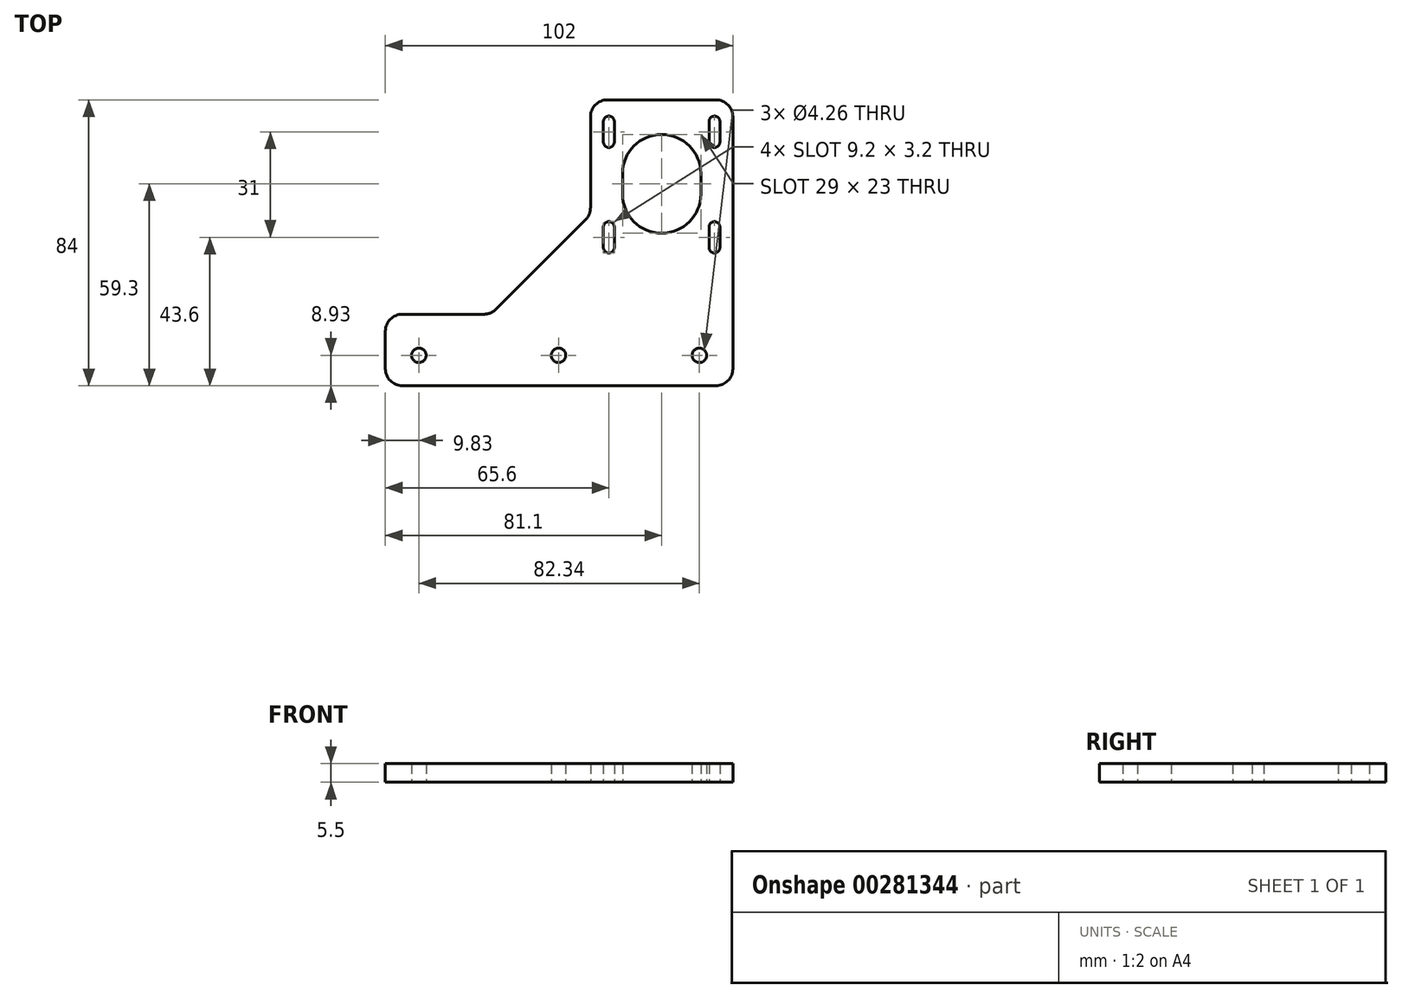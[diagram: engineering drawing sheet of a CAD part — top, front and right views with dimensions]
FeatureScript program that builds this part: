
annotation { "Feature Type Name" : "Feature", "Feature Type Description" : "" }
export const myFeature = defineFeature(function(context is Context, id is Id, definition is map)
    precondition{}
    {
        {
            var Q0;
            Q0=qCreatedBy(makeId("Top.planeOp"),FACE);
            var sketch = newSketch(context, id + "F0", { "sketchPlane" : qUnion([Q0])});
            skArc(sketch, "E0", {"start": v(16.2, 35.6) * mm, "mid": v(14.6, 37.2) * mm, "end": v(13, 35.6) * mm});
            skLineSegment(sketch, "E1", {"start": v(13, 35.6) * mm, "end": v(13, 29.6) * mm});
            skArc(sketch, "E2", {"start": v(13, 29.6) * mm, "mid": v(14.6, 28) * mm, "end": v(16.2, 29.6) * mm});
            skLineSegment(sketch, "E3", {"start": v(16.2, 29.6) * mm, "end": v(16.2, 35.6) * mm});
            skArc(sketch, "E4", {"start": v(7.74, 6.74) * mm, "mid": v(8.82, 8.36) * mm, "end": v(9.2, 10.27) * mm});
            skLineSegment(sketch, "E5", {"start": v(9.2, 10.27) * mm, "end": v(9.2, 37) * mm});
            skArc(sketch, "E6", {"start": v(9.2, 37) * mm, "mid": v(10.67, 40.53) * mm, "end": v(14.2, 42) * mm});
            skLineSegment(sketch, "E7", {"start": v(14.2, 42) * mm, "end": v(46, 42) * mm});
            skArc(sketch, "E8", {"start": v(46, 42) * mm, "mid": v(49.53, 40.53) * mm, "end": v(51, 37) * mm});
            skLineSegment(sketch, "E9", {"start": v(51, 37) * mm, "end": v(51, -37) * mm});
            skArc(sketch, "E10", {"start": v(51, -37) * mm, "mid": v(49.53, -40.53) * mm, "end": v(46, -42) * mm});
            skLineSegment(sketch, "E11", {"start": v(46, -42) * mm, "end": v(-46, -42) * mm});
            skArc(sketch, "E12", {"start": v(-46, -42) * mm, "mid": v(-49.53, -40.53) * mm, "end": v(-51, -37) * mm});
            skLineSegment(sketch, "E13", {"start": v(-51, -37) * mm, "end": v(-51, -26) * mm});
            skArc(sketch, "E14", {"start": v(-51, -26) * mm, "mid": v(-49.53, -22.47) * mm, "end": v(-46, -21) * mm});
            skLineSegment(sketch, "E15", {"start": v(-46, -21) * mm, "end": v(-22.07, -21) * mm});
            skArc(sketch, "E16", {"start": v(-22.07, -21) * mm, "mid": v(-20.16, -20.62) * mm, "end": v(-18.54, -19.54) * mm});
            skLineSegment(sketch, "E17", {"start": v(-18.54, -19.54) * mm, "end": v(7.74, 6.74) * mm});
            skLineSegment(sketch, "E18", {"start": v(47.2, 29.6) * mm, "end": v(47.2, 35.6) * mm});
            skArc(sketch, "E19", {"start": v(47.2, 35.6) * mm, "mid": v(45.6, 37.2) * mm, "end": v(44, 35.6) * mm});
            skLineSegment(sketch, "E20", {"start": v(44, 35.6) * mm, "end": v(44, 29.6) * mm});
            skArc(sketch, "E21", {"start": v(44, 29.6) * mm, "mid": v(45.6, 28) * mm, "end": v(47.2, 29.6) * mm});
            skArc(sketch, "E22", {"start": v(18.6, 14.3) * mm, "mid": v(30.1, 2.8) * mm, "end": v(41.6, 14.3) * mm});
            skLineSegment(sketch, "E23", {"start": v(41.6, 14.3) * mm, "end": v(41.6, 20.3) * mm});
            skArc(sketch, "E24", {"start": v(41.6, 20.3) * mm, "mid": v(30.1, 31.8) * mm, "end": v(18.6, 20.3) * mm});
            skLineSegment(sketch, "E25", {"start": v(18.6, 20.3) * mm, "end": v(18.6, 14.3) * mm});
            skCircle(sketch, "E26", {"center": v(41.17, -33.07) * mm, "radius": 2.13 * mm});
            skArc(sketch, "E27", {"start": v(16.2, 4.6) * mm, "mid": v(14.6, 6.2) * mm, "end": v(13, 4.6) * mm});
            skLineSegment(sketch, "E28", {"start": v(13, 4.6) * mm, "end": v(13, -1.4) * mm});
            skArc(sketch, "E29", {"start": v(13, -1.4) * mm, "mid": v(14.6, -3) * mm, "end": v(16.2, -1.4) * mm});
            skLineSegment(sketch, "E30", {"start": v(16.2, -1.4) * mm, "end": v(16.2, 4.6) * mm});
            skLineSegment(sketch, "E31", {"start": v(47.2, -1.4) * mm, "end": v(47.2, 4.6) * mm});
            skArc(sketch, "E32", {"start": v(47.2, 4.6) * mm, "mid": v(45.6, 6.2) * mm, "end": v(44, 4.6) * mm});
            skLineSegment(sketch, "E33", {"start": v(44, 4.6) * mm, "end": v(44, -1.4) * mm});
            skArc(sketch, "E34", {"start": v(44, -1.4) * mm, "mid": v(45.6, -3) * mm, "end": v(47.2, -1.4) * mm});
            skCircle(sketch, "E35", {"center": v(-0.17, -33.07) * mm, "radius": 2.13 * mm});
            skCircle(sketch, "E36", {"center": v(-41.17, -33.07) * mm, "radius": 2.13 * mm});
            skSolve(sketch);
        }
        {
            var Q0;
            Q0=makeQuery(id+"F0.imprint","IMPRINT",FACE,{"disambiguationData":[TD([[makeQuery(id+"F0.imprint","IMPRINT",EDGE,{"derivedFrom":sQuery(id+"F0.wireOp",EDGE,"E0")}),-1.0]])]});
            var Q1;
            Q1=sQuery(id+"F0.wireOp",EDGE,"E17");
            var Q2;
            Q2=sQuery(id+"F0.wireOp",EDGE,"E16");
            var Q3;
            Q3=sQuery(id+"F0.wireOp",EDGE,"E15");
            var Q4;
            Q4=sQuery(id+"F0.wireOp",EDGE,"E14");
            var Q5;
            Q5=sQuery(id+"F0.wireOp",EDGE,"E13");
            var Q6;
            Q6=sQuery(id+"F0.wireOp",EDGE,"E12");
            var Q7;
            Q7=sQuery(id+"F0.wireOp",EDGE,"E11");
            var Q8;
            Q8=sQuery(id+"F0.wireOp",EDGE,"E9");
            var Q9;
            Q9=sQuery(id+"F0.wireOp",EDGE,"E8");
            var Q10;
            Q10=sQuery(id+"F0.wireOp",EDGE,"E10");
            var Q11;
            Q11=sQuery(id+"F0.wireOp",EDGE,"E6");
            var Q12;
            Q12=sQuery(id+"F0.wireOp",EDGE,"E7");
            var Q13;
            Q13=sQuery(id+"F0.wireOp",EDGE,"E5");
            var Q14;
            Q14=sQuery(id+"F0.wireOp",EDGE,"E4");
            var Q15;
            Q15=sQuery(id+"F0.wireOp",EDGE,"E24");
            var Q16;
            Q16=sQuery(id+"F0.wireOp",EDGE,"E22");
            var Q17;
            Q17=sQuery(id+"F0.wireOp",EDGE,"E23");
            var Q18;
            Q18=sQuery(id+"F0.wireOp",EDGE,"E25");
            var Q19;
            Q19=sQuery(id+"F0.wireOp",EDGE,"E2");
            var Q20;
            Q20=sQuery(id+"F0.wireOp",EDGE,"E3");
            var Q21;
            Q21=sQuery(id+"F0.wireOp",EDGE,"E0");
            var Q22;
            Q22=sQuery(id+"F0.wireOp",EDGE,"E1");
            var Q23;
            Q23=sQuery(id+"F0.wireOp",EDGE,"E29");
            var Q24;
            Q24=sQuery(id+"F0.wireOp",EDGE,"E30");
            var Q25;
            Q25=sQuery(id+"F0.wireOp",EDGE,"E27");
            var Q26;
            Q26=sQuery(id+"F0.wireOp",EDGE,"E28");
            var Q27;
            Q27=sQuery(id+"F0.wireOp",EDGE,"E34");
            var Q28;
            Q28=sQuery(id+"F0.wireOp",EDGE,"E31");
            var Q29;
            Q29=sQuery(id+"F0.wireOp",EDGE,"E33");
            var Q30;
            Q30=sQuery(id+"F0.wireOp",EDGE,"E32");
            var Q31;
            Q31=sQuery(id+"F0.wireOp",EDGE,"E18");
            var Q32;
            Q32=sQuery(id+"F0.wireOp",EDGE,"E20");
            var Q33;
            Q33=sQuery(id+"F0.wireOp",EDGE,"E19");
            var Q34;
            Q34=sQuery(id+"F0.wireOp",EDGE,"E21");
            var Q35;
            Q35=sQuery(id+"F0.wireOp",EDGE,"E26");
            var Q36;
            Q36=sQuery(id+"F0.wireOp",EDGE,"E35");
            var Q37;
            Q37=sQuery(id+"F0.wireOp",EDGE,"E36");
            extrude(context, id + "F1", {"entities" : qUnion([Q0]), "surfaceEntities" : qUnion([Q1, Q2, Q3, Q4, Q5, Q6, Q7, Q8, Q9, Q10, Q11, Q12, Q13, Q14, Q15, Q16, Q17, Q18, Q19, Q20, Q21, Q22, Q23, Q24, Q25, Q26, Q27, Q28, Q29, Q30, Q31, Q32, Q33, Q34, Q35, Q36, Q37]), "depth" : 5.5 * mm});
        }
    });
